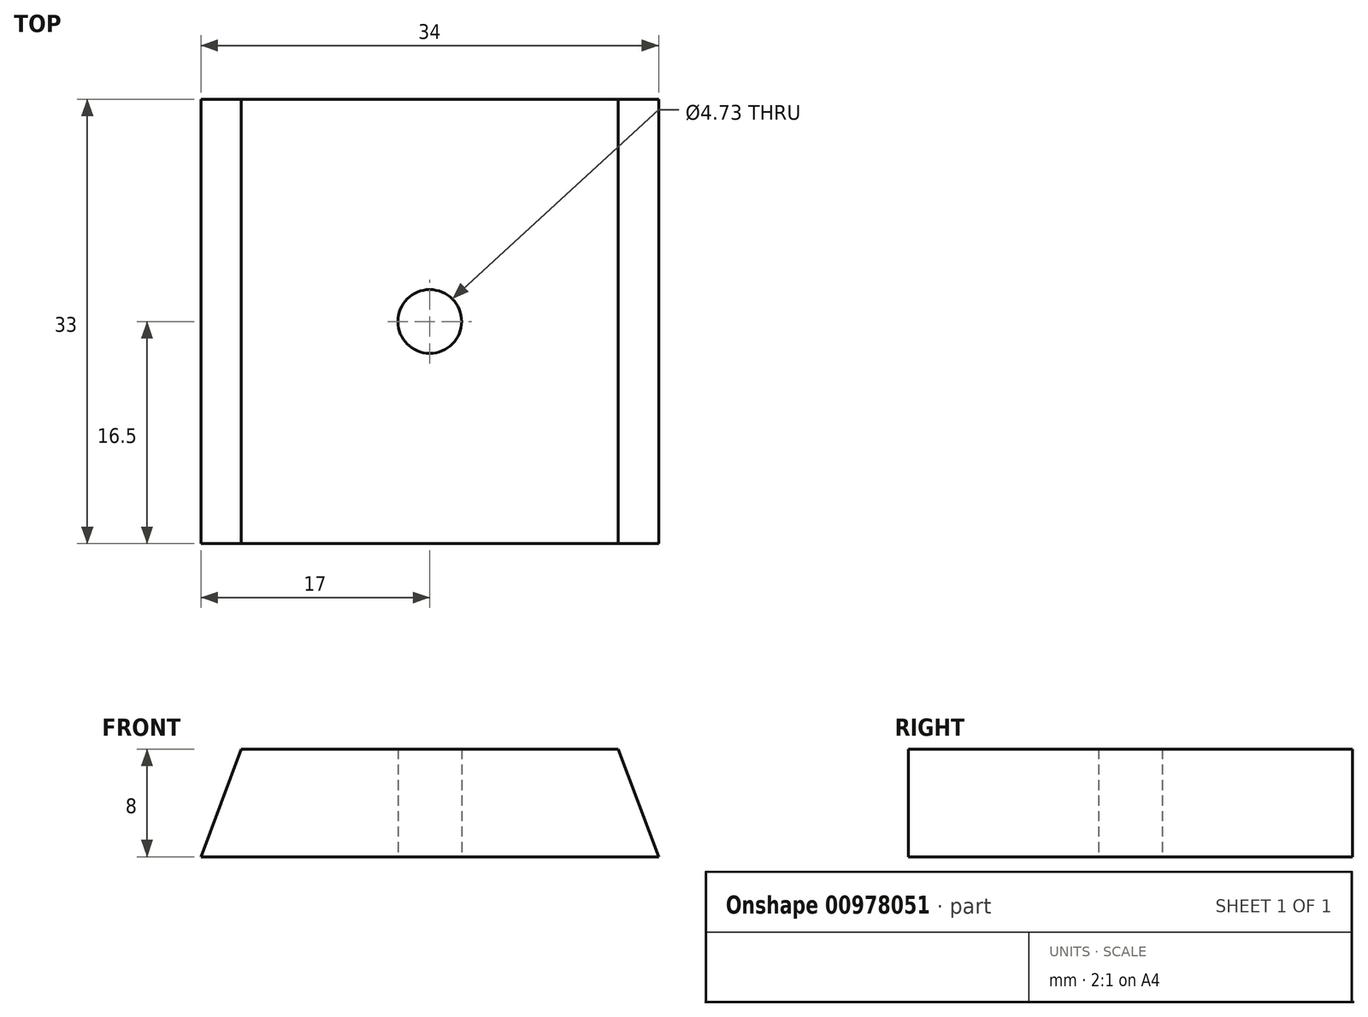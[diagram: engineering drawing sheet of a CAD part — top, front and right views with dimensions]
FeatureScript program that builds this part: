
annotation { "Feature Type Name" : "Feature", "Feature Type Description" : "" }
export const myFeature = defineFeature(function(context is Context, id is Id, definition is map)
    precondition{}
    {
        {
            var Q0;
            Q0=qCreatedBy(makeId("Top.planeOp"),FACE);
            var sketch = newSketch(context, id + "F0", { "sketchPlane" : qUnion([Q0])});
            skLineSegment(sketch, "E0.bottom", {"start": v(17, -16.5) * mm, "end": v(-17, -16.5) * mm});
            skLineSegment(sketch, "E0.top", {"start": v(17, 16.5) * mm, "end": v(-17, 16.5) * mm});
            skLineSegment(sketch, "E0.left", {"start": v(17, -16.5) * mm, "end": v(17, 16.5) * mm});
            skLineSegment(sketch, "E0.right", {"start": v(-17, -16.5) * mm, "end": v(-17, 16.5) * mm});
            skPoint(sketch, "E0.middle", {"position": v(0, 0) * mm});
            skCircle(sketch, "E1", {"center": v(0, 0) * mm, "radius": 2.37 * mm});
            skSolve(sketch);
        }
        {
            var Q0;
            Q0=makeQuery(id+"F0.imprint","IMPRINT",FACE,{"disambiguationData":[TD([[makeQuery(id+"F0.imprint","IMPRINT",EDGE,{"derivedFrom":sQuery(id+"F0.wireOp",EDGE,"E0.bottom")}),-1.0]])]});
            extrude(context, id + "F1", {"entities" : qUnion([Q0]), "depth" : 8 * mm, "offsetDistance" : 25 * mm});
        }
        {
            var Q0;
            Q0=makeQuery(id+"F1.opExtrude","SWEPT_FACE",FACE,{"disambiguationData":[OSD([sQuery(id+"F0.wireOp",EDGE,"E0.bottom")])]});
            var sketch = newSketch(context, id + "F2", { "sketchPlane" : qUnion([Q0])});
            skLineSegment(sketch, "E2", {"start": v(-14, 8) * mm, "end": v(-17, 0) * mm});
            skLineSegment(sketch, "E3", {"start": v(14, 8) * mm, "end": v(17, 0) * mm});
            skLineSegment(sketch, "E4", {"start": v(14, 8) * mm, "end": v(17, 8) * mm});
            skLineSegment(sketch, "E5", {"start": v(17, 8) * mm, "end": v(17, 0) * mm});
            skLineSegment(sketch, "E6", {"start": v(-14, 8) * mm, "end": v(-17, 8) * mm});
            skLineSegment(sketch, "E7", {"start": v(-17, 8) * mm, "end": v(-17, 0) * mm});
            skSolve(sketch);
        }
        {
            var Q0;
            Q0=makeQuery(id+"F2.imprint","IMPRINT",FACE,{"disambiguationData":[TD([[makeQuery(id+"F2.imprint","IMPRINT",EDGE,{"derivedFrom":sQuery(id+"F2.wireOp",EDGE,"E2")}),-1.0]])]});
            var Q1;
            Q1=makeQuery(id+"F2.imprint","IMPRINT",FACE,{"disambiguationData":[TD([[makeQuery(id+"F2.imprint","IMPRINT",EDGE,{"derivedFrom":sQuery(id+"F2.wireOp",EDGE,"E3")}),1.0]])]});
            extrude(context, id + "F3", {"entities" : qUnion([Q0, Q1]), "operationType" : NewBodyOperationType.REMOVE, "oppositeDirection" : true, "depth" : 35 * mm, "offsetDistance" : 25 * mm});
        }
    });
